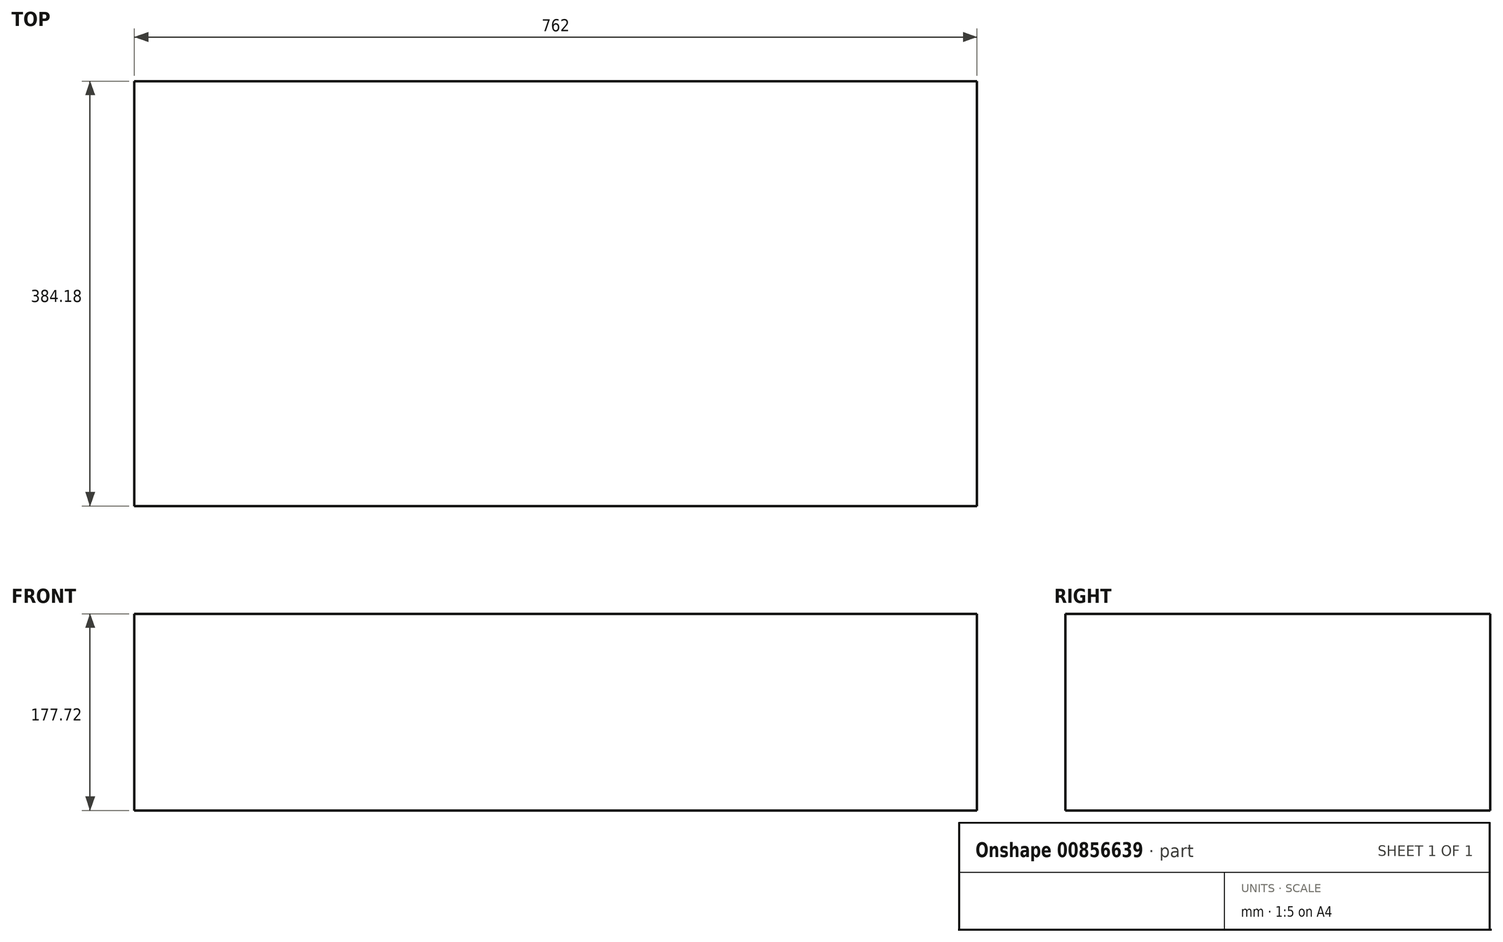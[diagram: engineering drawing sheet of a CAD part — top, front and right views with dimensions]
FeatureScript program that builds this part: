
annotation { "Feature Type Name" : "Feature", "Feature Type Description" : "" }
export const myFeature = defineFeature(function(context is Context, id is Id, definition is map)
    precondition{}
    {
        {
            var Q0;
            Q0=qCreatedBy(makeId("Front.planeOp"),FACE);
            var sketch = newSketch(context, id + "F0", { "sketchPlane" : qUnion([Q0])});
            skLineSegment(sketch, "E0.bottom", {"start": v(1208.67, 0) * mm, "end": v(2113.54, 0) * mm});
            skLineSegment(sketch, "E0.top", {"start": v(1208.67, 1778) * mm, "end": v(2113.54, 1778) * mm});
            skLineSegment(sketch, "E0.left", {"start": v(1208.67, 0) * mm, "end": v(1208.67, 1778) * mm});
            skLineSegment(sketch, "E0.right", {"start": v(2113.54, 0) * mm, "end": v(2113.54, 1778) * mm});
            skLineSegment(sketch, "E1.left", {"start": v(0, 0) * mm, "end": v(0.1, 863.6) * mm});
            skLineSegment(sketch, "E1.right", {"start": v(-1905, -2.15) * mm, "end": v(-1904.9, 861.45) * mm});
            skLineSegment(sketch, "E2.top", {"start": v(0.1, 901.7) * mm, "end": v(-2504.34, 901.7) * mm});
            skLineSegment(sketch, "E2.left", {"start": v(0.1, 863.6) * mm, "end": v(0.1, 901.7) * mm});
            skLineSegment(sketch, "E2.right", {"start": v(-2504.34, 863.6) * mm, "end": v(-2504.34, 901.7) * mm});
            skLineSegment(sketch, "E3", {"start": v(-1904.9, 1058.57) * mm, "end": v(-1904.9, -228.77) * mm, "construction": true});
            skLineSegment(sketch, "E4", {"start": v(0, 1058.57) * mm, "end": v(0, -228.77) * mm, "construction": true});
            skLineSegment(sketch, "E5.bottom", {"start": v(0, 0) * mm, "end": v(-381, 0) * mm});
            skLineSegment(sketch, "E5.left", {"start": v(0, 0) * mm, "end": v(0, 857.25) * mm});
            skLineSegment(sketch, "E6", {"start": v(-381, 0) * mm, "end": v(-387.35, 0) * mm, "construction": true});
            skLineSegment(sketch, "E7.bottom", {"start": v(-387.35, 0) * mm, "end": v(-1143, 0) * mm, "construction": true});
            skLineSegment(sketch, "E7.left", {"start": v(-387.35, 0) * mm, "end": v(-387.35, 736.6) * mm, "construction": true});
            skLineSegment(sketch, "E8", {"start": v(0, 0) * mm, "end": v(-1905, -2.15) * mm, "construction": true});
            skLineSegment(sketch, "E9.bottom", {"start": v(-387.35, 857.25) * mm, "end": v(-1143, 857.25) * mm, "construction": true});
            skLineSegment(sketch, "E9.top", {"start": v(-387.35, 121.5) * mm, "end": v(-1143, 120.65) * mm, "construction": true});
            skLineSegment(sketch, "E9.left", {"start": v(-387.35, 857.25) * mm, "end": v(-387.35, 121.5) * mm, "construction": true});
            skLineSegment(sketch, "E9.right", {"start": v(-1143, 857.25) * mm, "end": v(-1143, 120.65) * mm, "construction": true});
            skLineSegment(sketch, "E10", {"start": v(-1149.35, 857.25) * mm, "end": v(-1149.35, 120.65) * mm, "construction": true});
            skLineSegment(sketch, "E11.bottom", {"start": v(-1149.35, 857.25) * mm, "end": v(-1527.18, 857.25) * mm});
            skLineSegment(sketch, "E11.top", {"start": v(-1149.35, 82.55) * mm, "end": v(-1527.18, 82.55) * mm});
            skLineSegment(sketch, "E11.left", {"start": v(-1149.35, 857.25) * mm, "end": v(-1149.35, 82.55) * mm});
            skLineSegment(sketch, "E11.right", {"start": v(-1527.18, 857.25) * mm, "end": v(-1527.18, 82.55) * mm});
            skLineSegment(sketch, "E12", {"start": v(-1527.18, 82.55) * mm, "end": v(-1533.53, 82.54) * mm, "construction": true});
            skLineSegment(sketch, "E13.bottom", {"start": v(-1533.53, 82.54) * mm, "end": v(-1911.35, 82.54) * mm});
            skLineSegment(sketch, "E13.top", {"start": v(-1533.53, 857.25) * mm, "end": v(-1911.35, 857.25) * mm});
            skLineSegment(sketch, "E13.left", {"start": v(-1533.53, 82.54) * mm, "end": v(-1533.53, 857.25) * mm});
            skLineSegment(sketch, "E13.right", {"start": v(-1911.35, 82.54) * mm, "end": v(-1911.35, 857.25) * mm});
            skLineSegment(sketch, "E14", {"start": v(0, 857.25) * mm, "end": v(-2682.58, 857.25) * mm, "construction": true});
            skLineSegment(sketch, "E15.bottom", {"start": v(0, 857.25) * mm, "end": v(-381, 857.25) * mm});
            skLineSegment(sketch, "E15.top", {"start": v(0, 82.55) * mm, "end": v(-381, 82.55) * mm});
            skLineSegment(sketch, "E15.left", {"start": v(0, 857.25) * mm, "end": v(0, 82.55) * mm});
            skLineSegment(sketch, "E15.right", {"start": v(-381, 857.25) * mm, "end": v(-381, 82.55) * mm});
            skLineSegment(sketch, "E16.bottom", {"start": v(-387.35, 82.55) * mm, "end": v(-1143, 82.55) * mm});
            skLineSegment(sketch, "E16.top", {"start": v(-387.35, 115.22) * mm, "end": v(-1143, 115.22) * mm});
            skLineSegment(sketch, "E16.left", {"start": v(-387.35, 82.55) * mm, "end": v(-387.35, 115.22) * mm});
            skLineSegment(sketch, "E16.right", {"start": v(-1143, 82.55) * mm, "end": v(-1143, 115.22) * mm});
            skPoint(sketch, "E17", {"position": v(-765.18, 121.08) * mm});
            skPoint(sketch, "E18", {"position": v(-1530.35, 82.55) * mm});
            skPoint(sketch, "E18.positionSnap0", {"position": v(-1530.35, 82.55) * mm});
            skLineSegment(sketch, "E19.bottom", {"start": v(0, 0) * mm, "end": v(-3447.41, 0) * mm});
            skLineSegment(sketch, "E19.top", {"start": v(0, 2438.4) * mm, "end": v(-3447.42, 2438.4) * mm});
            skLineSegment(sketch, "E19.left", {"start": v(0, 0) * mm, "end": v(0, 2438.4) * mm});
            skLineSegment(sketch, "E19.right", {"start": v(-3447.41, 0) * mm, "end": v(-3447.42, 2438.4) * mm});
            skLineSegment(sketch, "E20.bottom", {"start": v(-2504.34, 0) * mm, "end": v(-2542.44, 0) * mm});
            skLineSegment(sketch, "E20.top", {"start": v(-2504.34, 2438.4) * mm, "end": v(-2542.44, 2438.4) * mm});
            skLineSegment(sketch, "E20.left", {"start": v(-2504.34, 0) * mm, "end": v(-2504.34, 2438.4) * mm});
            skLineSegment(sketch, "E20.right", {"start": v(-2542.44, 0) * mm, "end": v(-2542.44, 2438.4) * mm});
            skLineSegment(sketch, "E21", {"start": v(-3447.31, 2438.4) * mm, "end": v(-3447.31, 0) * mm, "construction": true});
            skLineSegment(sketch, "E22.bottom", {"start": v(-3447.31, 2438.4) * mm, "end": v(-3485.52, 2438.4) * mm});
            skLineSegment(sketch, "E22.top", {"start": v(-3447.31, 0) * mm, "end": v(-3485.51, 0) * mm});
            skLineSegment(sketch, "E22.left", {"start": v(-3447.31, 2438.4) * mm, "end": v(-3447.31, 0) * mm});
            skLineSegment(sketch, "E22.right", {"start": v(-3485.52, 2438.4) * mm, "end": v(-3485.51, 0) * mm});
            skLineSegment(sketch, "E23", {"start": v(-3447.31, 1778) * mm, "end": v(-2542.44, 1778) * mm});
            skLineSegment(sketch, "E24", {"start": v(-765.18, 121.08) * mm, "end": v(-765.18, 1778) * mm, "construction": true});
            skPoint(sketch, "E25.middle", {"position": v(-765.18, 1778) * mm});
            skLineSegment(sketch, "E26.bottom", {"start": v(-2504.34, 2438.4) * mm, "end": v(-1146.18, 2438.4) * mm});
            skLineSegment(sketch, "E26.top", {"start": v(-2504.34, 1778) * mm, "end": v(-1146.18, 1778) * mm});
            skLineSegment(sketch, "E26.left", {"start": v(-2504.34, 2438.4) * mm, "end": v(-2504.34, 1778) * mm});
            skLineSegment(sketch, "E26.right", {"start": v(-1146.18, 2438.4) * mm, "end": v(-1146.18, 1778) * mm});
            skLineSegment(sketch, "E27.bottom", {"start": v(0, 2438.4) * mm, "end": v(-384.18, 2438.4) * mm});
            skLineSegment(sketch, "E27.top", {"start": v(0, 1778) * mm, "end": v(-384.18, 1778) * mm});
            skLineSegment(sketch, "E27.left", {"start": v(0, 2438.4) * mm, "end": v(0, 1778) * mm});
            skLineSegment(sketch, "E27.right", {"start": v(-384.18, 2438.4) * mm, "end": v(-384.18, 1778) * mm});
            skLineSegment(sketch, "E28.bottom", {"start": v(-1146.18, 2133.52) * mm, "end": v(-384.18, 2133.52) * mm});
            skLineSegment(sketch, "E28.top", {"start": v(-1146.18, 1955.8) * mm, "end": v(-384.18, 1955.8) * mm});
            skLineSegment(sketch, "E28.left", {"start": v(-1146.18, 2133.52) * mm, "end": v(-1146.18, 1955.8) * mm});
            skLineSegment(sketch, "E28.right", {"start": v(-384.18, 2133.52) * mm, "end": v(-384.18, 1955.8) * mm});
            skLineSegment(sketch, "E29.top", {"start": v(-2504.34, 1524) * mm, "end": v(-1146.18, 1524) * mm});
            skLineSegment(sketch, "E29.left", {"start": v(-2504.34, 1778) * mm, "end": v(-2504.34, 1524) * mm});
            skLineSegment(sketch, "E29.right", {"start": v(-1146.18, 1778) * mm, "end": v(-1146.18, 1524) * mm});
            skLineSegment(sketch, "E30.bottom", {"start": v(-384.18, 1778) * mm, "end": v(0, 1778) * mm});
            skLineSegment(sketch, "E30.top", {"start": v(-384.18, 1524) * mm, "end": v(0, 1524) * mm});
            skLineSegment(sketch, "E30.left", {"start": v(-384.18, 1778) * mm, "end": v(-384.18, 1524) * mm});
            skLineSegment(sketch, "E30.right", {"start": v(0, 1778) * mm, "end": v(0, 1524) * mm});
            skLineSegment(sketch, "E31.0", {"start": v(-1171.58, 1778) * mm, "end": v(-1171.58, 1549.4) * mm});
            skLineSegment(sketch, "E31.1", {"start": v(-2504.34, 1549.4) * mm, "end": v(-1171.58, 1549.4) * mm});
            skLineSegment(sketch, "E32.0", {"start": v(-358.78, 1549.4) * mm, "end": v(0, 1549.4) * mm});
            skLineSegment(sketch, "E32.1", {"start": v(-358.78, 1778) * mm, "end": v(-358.78, 1549.4) * mm});
            skLineSegment(sketch, "E33", {"start": v(-25.4, 1549.4) * mm, "end": v(-25.4, 1778) * mm});
            skSolve(sketch);
        }
        {
            var Q0;
            Q0=makeQuery(id+"F0.imprint","IMPRINT",FACE,{"disambiguationData":[TD([[makeQuery(id+"F0.imprint","IMPRINT",EDGE,{"derivedFrom":sQuery(id+"F0.wireOp",EDGE,"E28.bottom")}),-1.0]])]});
            extrude(context, id + "F1", {"entities" : qUnion([Q0]), "oppositeDirection" : true, "depth" : 609.6 * mm, "offsetDistance" : 25.4 * mm, "hasSecondDirection" : true, "secondDirectionOppositeDirection" : true, "secondDirectionDepth" : 225.42 * mm});
        }
    });
